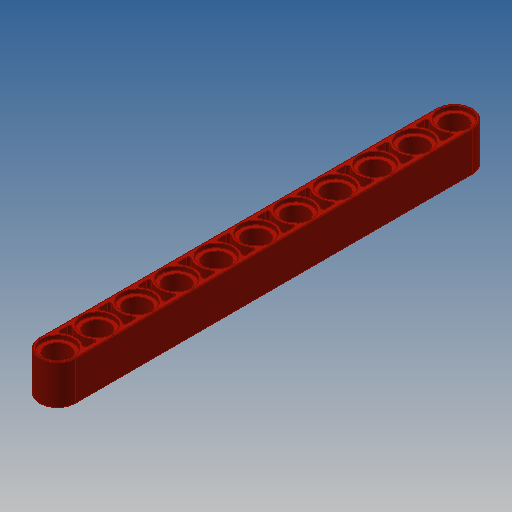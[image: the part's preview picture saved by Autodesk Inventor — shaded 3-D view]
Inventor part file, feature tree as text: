
AUTODESK INVENTOR PART (.ipt)
format: ipt  version: 2022.2 (Build 262287000, 287)  size: 446,464 bytes
history: native  units: mm
features: extrude x3, sketch x2, mirror x1, fillet x1
ambient origin geometry x8: Origin, YZ Plane, XZ Plane, XY Plane, X Axis, Y Axis, Z Axis, Center Point
bodies: Solid1 (feature_tree)
feature tree (7):
  extrude  "Extrusion1"  Depth=7.2mm
  sketch  "Sketch6"  dims[d41=0.8mm d42=0.0mm d43=3.1mm d44=0.0mm d48=80.0mm d49=6.4mm d50=4.8mm d51=8.0mm d52=0.8mm d53=100.0mm d55=8.0mm d56=10.0mm d58=10.0mm d60=0.4mm d61=0.1mm]
  extrude  "Extrusion7"  Depth=3.1mm TaperAngle=0.0deg
  extrude  "Extrusion8"  Depth=0.1mm
  mirror  "Mirror1"
  fillet  "Fillet2"  Radius=6.4mm
  sketch  "Sketch1"  dims[d14=8.0mm d15=0.0mm d32=7.2mm]
